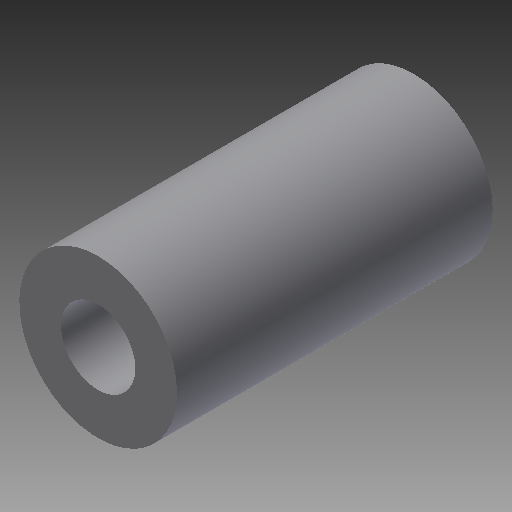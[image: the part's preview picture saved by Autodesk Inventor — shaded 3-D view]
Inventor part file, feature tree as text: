
AUTODESK INVENTOR PART (.ipt)
format: ipt  version: 2019.4 (Build 234330000, 330)  size: 120,320 bytes
history: native  units: in
note: dims shown in document units (in); Inventor stores cm internally (conversion verified against a paired STEP export)
features: other x7, sketch x2, revolve x1, hole x1
ambient origin geometry x8: Origin, YZ Plane, XZ Plane, XY Plane, X Axis, Y Axis, Z Axis, Center Point
bodies: Solid1 (feature_tree)
feature tree (11):
  revolve  "Revolution1"  [1 undecoded]
  hole  "Hole1"  [1 undecoded]
  other  "screw_XY"
  other  "screw_YZ"
  other  "screw_ZX"
  other  "screw_X"
  other  "screw_Y"
  other  "screw_Z"
  other  "screw_Center"
  sketch  "Sketch_1"  dims[d0=360.0deg]
  sketch  "Sketch2"  dims[d1=0.147in d2=0.75in d3=0.375in d4=0.25in d5=0.5635in d6=0.625in d7=0.0in d8=0.0in]
note: 2 required parameter values undecoded (feature->parameter linkage not recoverable at this tier; creation-order binding heuristic only, values carry confidence <= 0.55)